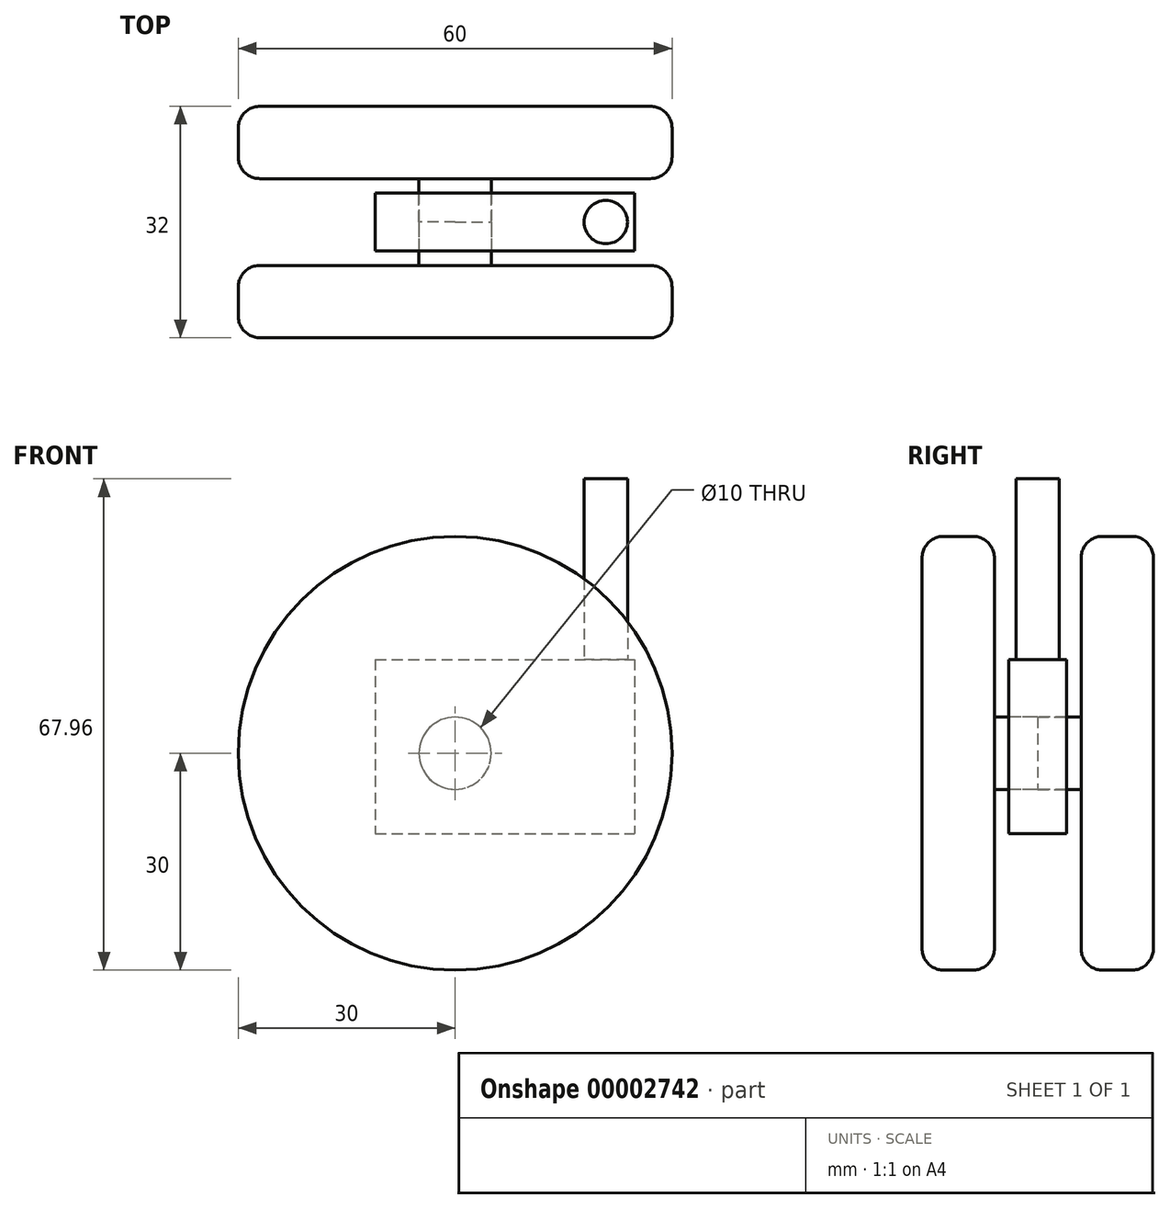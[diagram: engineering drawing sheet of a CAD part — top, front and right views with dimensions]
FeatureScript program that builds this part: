
annotation { "Feature Type Name" : "Feature", "Feature Type Description" : "" }
export const myFeature = defineFeature(function(context is Context, id is Id, definition is map)
    precondition{}
    {
        {
            var Q0;
            Q0=qCreatedBy(makeId("Front.planeOp"),FACE);
            var sketch = newSketch(context, id + "F0", { "sketchPlane" : qUnion([Q0])});
            skCircle(sketch, "E0", {"center": v(0, 0) * mm, "radius": 30 * mm});
            skSolve(sketch);
        }
        {
            var Q0;
            Q0=makeQuery(id+"F0.imprint","IMPRINT",FACE,{"disambiguationData":[TD([[makeQuery(id+"F0.imprint","IMPRINT",EDGE,{"derivedFrom":sQuery(id+"F0.wireOp",EDGE,"E0")}),1.0]])]});
            extrude(context, id + "F1", {"entities" : qUnion([Q0]), "depth" : 10 * mm});
        }
        {
            var Q0;
            Q0=makeQuery(id+"F1.opExtrude","CAP_EDGE",EDGE,{"disambiguationData":[OSD([sQuery(id+"F0.wireOp",EDGE,"E0")])],"isStart":true});
            var Q1;
            Q1=makeQuery(id+"F1.opExtrude","CAP_EDGE",EDGE,{"disambiguationData":[OSD([sQuery(id+"F0.wireOp",EDGE,"E0")])],"isStart":false});
            fillet(context, id + "F2", {"entities" : qUnion([Q0, Q1]), "radius" : 3 * mm, "tangentPropagation" : true, "allowEdgeOverflow" : false});
        }
        {
            var Q0;
            Q0=makeQuery(id+"F1.opExtrude","CAP_FACE",FACE,{"disambiguationData":[OSD([sQuery(id+"F0.wireOp",EDGE,"E0")])],"isStart":true});
            var sketch = newSketch(context, id + "F3", { "sketchPlane" : qUnion([Q0])});
            skCircle(sketch, "E1", {"center": v(0, 0) * mm, "radius": 5 * mm});
            skSolve(sketch);
        }
        {
            var Q0;
            Q0=makeQuery(id+"F3.imprint","IMPRINT",FACE,{"disambiguationData":[TD([[makeQuery(id+"F3.imprint","IMPRINT",EDGE,{"derivedFrom":sQuery(id+"F3.wireOp",EDGE,"E1")}),1.0]])]});
            extrude(context, id + "F4", {"entities" : qUnion([Q0]), "operationType" : NewBodyOperationType.ADD, "depth" : 6 * mm});
        }
        {
            var Q0;
            Q0=makeQuery(id+"F1.opExtrude","SWEPT_BODY",BODY,{"disambiguationData":[OSD([sQuery(id+"F0.wireOp",EDGE,"E0")])]});
            var Q1;
            Q1=makeQuery(id+"F4.opExtrude","CAP_FACE",FACE,{"disambiguationData":[OSD([sQuery(id+"F3.wireOp",EDGE,"E1")])],"isStart":false});
            mirror(context, id + "F5", {"entities" : qUnion([Q0]), "mirrorPlane" : qUnion([Q1])});
        }
        {
            var Q0;
            Q0=makeQuery(id+"F4.opExtrude","CAP_FACE",FACE,{"disambiguationData":[OSD([sQuery(id+"F3.wireOp",EDGE,"E1")])],"isStart":false});
            var sketch = newSketch(context, id + "F6", { "sketchPlane" : qUnion([Q0])});
            skLineSegment(sketch, "E2.bottom", {"start": v(11.06, 12.96) * mm, "end": v(-24.84, 12.96) * mm});
            skLineSegment(sketch, "E2.top", {"start": v(11.06, -11.15) * mm, "end": v(-24.84, -11.15) * mm});
            skLineSegment(sketch, "E2.left", {"start": v(11.06, 12.96) * mm, "end": v(11.06, -11.15) * mm});
            skLineSegment(sketch, "E2.right", {"start": v(-24.84, 12.96) * mm, "end": v(-24.84, -11.15) * mm});
            skSolve(sketch);
        }
        {
            var Q0;
            Q0=makeQuery(id+"F6.imprint","IMPRINT",FACE,{"disambiguationData":[TD([[makeQuery(id+"F6.imprint","IMPRINT",EDGE,{"derivedFrom":sQuery(id+"F6.wireOp",EDGE,"E2.bottom")}),1.0]])]});
            extrude(context, id + "F7", {"entities" : qUnion([Q0]), "depth" : 8 * mm, "symmetric" : true});
        }
        {
            var Q0;
            Q0=makeQuery(id+"F7.opExtrude","SWEPT_FACE",FACE,{"disambiguationData":[OSD([sQuery(id+"F6.wireOp",EDGE,"E2.bottom")])]});
            var sketch = newSketch(context, id + "F8", { "sketchPlane" : qUnion([Q0])});
            skLineSegment(sketch, "E3", {"start": v(20.84, 10) * mm, "end": v(20.84, 2) * mm, "construction": true});
            skCircle(sketch, "E4", {"center": v(20.84, 6) * mm, "radius": 3 * mm});
            skSolve(sketch);
        }
        {
            var Q0;
            Q0=makeQuery(id+"F8.imprint","IMPRINT",FACE,{"disambiguationData":[TD([[makeQuery(id+"F8.imprint","IMPRINT",EDGE,{"derivedFrom":sQuery(id+"F8.wireOp",EDGE,"E4")}),1.0]])]});
            var Q1;
            Q1=sQuery(id+"F8.wireOp",EDGE,"E4");
            extrude(context, id + "F9", {"entities" : qUnion([Q0]), "operationType" : NewBodyOperationType.ADD, "surfaceEntities" : qUnion([Q1]), "depth" : 25 * mm});
        }
    });
